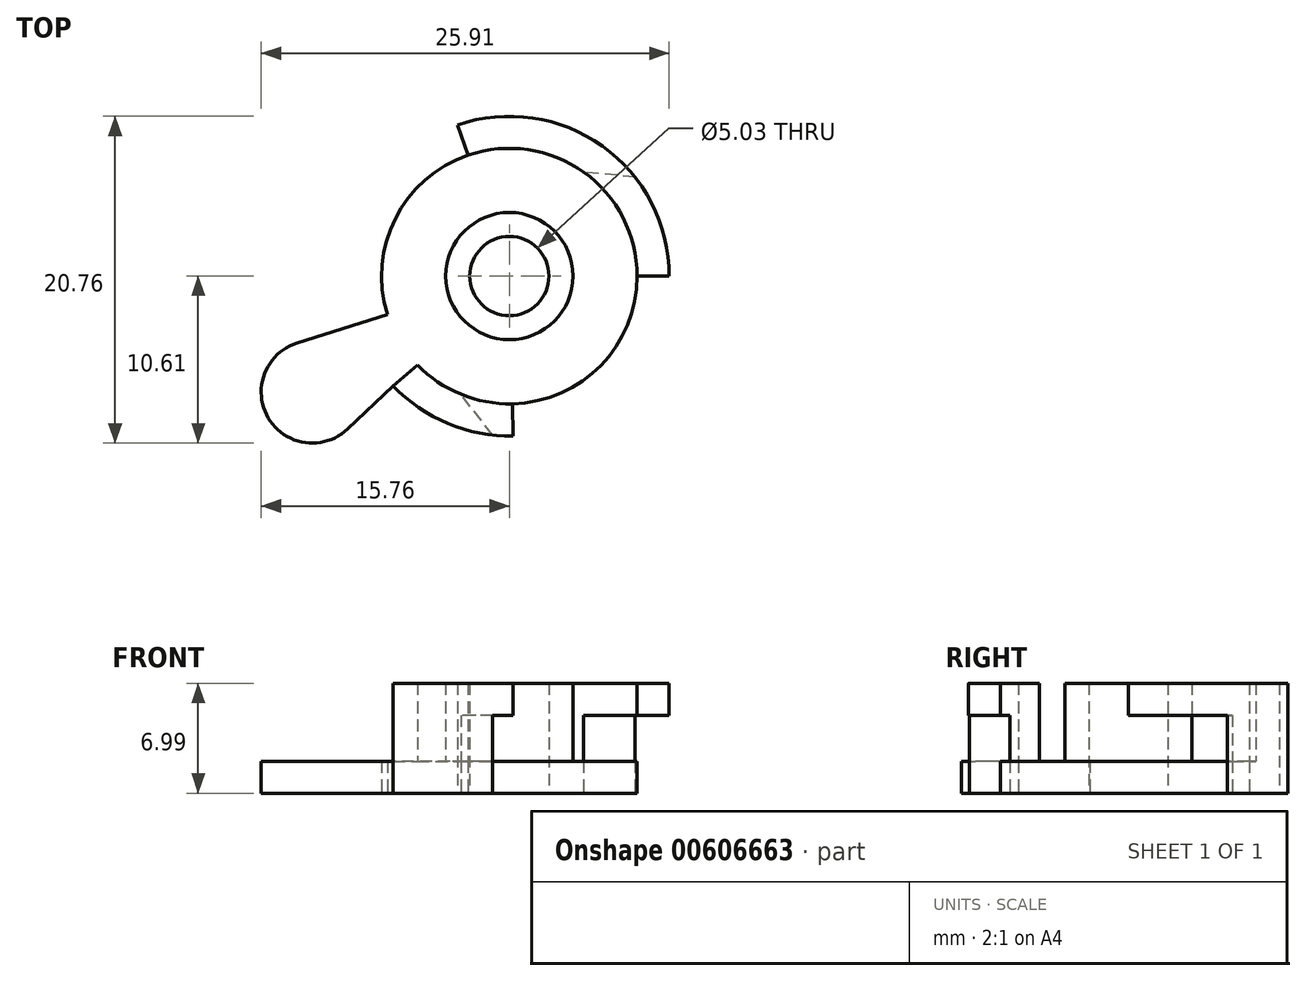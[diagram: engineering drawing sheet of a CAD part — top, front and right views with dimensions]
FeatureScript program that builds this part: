
annotation { "Feature Type Name" : "Feature", "Feature Type Description" : "" }
export const myFeature = defineFeature(function(context is Context, id is Id, definition is map)
    precondition{}
    {
        {
            var Q0;
            Q0=qCreatedBy(makeId("Top.planeOp"),FACE);
            var sketch = newSketch(context, id + "F0", { "sketchPlane" : qUnion([Q0])});
            skCircle(sketch, "E0", {"center": v(0, 0) * mm, "radius": 8.12 * mm});
            skCircle(sketch, "E1", {"center": v(0, 0) * mm, "radius": 2.51 * mm});
            skArc(sketch, "E2", {"start": v(10.15, 0) * mm, "mid": v(5.9, 8.26) * mm, "end": v(-3.28, 9.6) * mm});
            skLineSegment(sketch, "E3", {"start": v(-3.28, 9.6) * mm, "end": v(-2.63, 7.68) * mm});
            skLineSegment(sketch, "E4", {"start": v(10.15, 0) * mm, "end": v(8.12, 0) * mm});
            skArc(sketch, "E5", {"start": v(-9.68, -3.05) * mm, "mid": v(-5.9, -8.26) * mm, "end": v(0.24, -10.14) * mm});
            skLineSegment(sketch, "E6", {"start": v(-9.68, -3.05) * mm, "end": v(-7.74, -2.44) * mm});
            skLineSegment(sketch, "E7", {"start": v(-7.37, -6.97) * mm, "end": v(-10.28, -9.72) * mm});
            skLineSegment(sketch, "E8", {"start": v(-9.68, -3.05) * mm, "end": v(-13.5, -4.26) * mm});
            skLineSegment(sketch, "E9", {"start": v(0.24, -10.14) * mm, "end": v(0.2, -8.11) * mm});
            skLineSegment(sketch, "E10", {"start": v(-5.9, -8.26) * mm, "end": v(0, 0) * mm, "construction": true});
            skPoint(sketch, "E10.startSnap0", {"position": v(-5.9, -8.26) * mm});
            skLineSegment(sketch, "E11", {"start": v(5.9, 8.26) * mm, "end": v(0, 0) * mm, "construction": true});
            skLineSegment(sketch, "E12", {"start": v(-5.9, -8.26) * mm, "end": v(4.72, 6.6) * mm, "construction": true});
            skLineSegment(sketch, "E13", {"start": v(-8.75, -5.14) * mm, "end": v(-15.31, -9) * mm, "construction": true});
            skArc(sketch, "E14", {"start": v(-13.5, -4.26) * mm, "mid": v(-15.31, -9) * mm, "end": v(-10.28, -9.72) * mm});
            skSolve(sketch);
        }
        {
            var Q0;
            Q0=makeQuery(id+"F0.imprint","IMPRINT",FACE,{"disambiguationData":[TD([[makeQuery(id+"F0.imprint","IMPRINT",EDGE,{"derivedFrom":sQuery(id+"F0.wireOp",EDGE,"E1")}),-1.0]])]});
            var Q1;
            Q1=makeQuery(id+"F0.imprint","IMPRINT",FACE,{"disambiguationData":[TD([[makeQuery(id+"F0.imprint","IMPRINT",EDGE,{"derivedFrom":sQuery(id+"F0.wireOp",EDGE,"E2")}),1.0]])]});
            var Q2;
            {var subQ0=sQuery(id+"F0.wireOp",EDGE,"E6");Q2=makeQuery(id+"F0.imprint","IMPRINT",FACE,{"disambiguationData":[TD([[makeQuery(id+"F0.imprint","IMPRINT",EDGE,{"derivedFrom":subQ0}),-1.0]])]});}
            var Q3;
            {var subQ2=sQuery(id+"F0.wireOp",EDGE,"E7");Q3=makeQuery(id+"F0.imprint","IMPRINT",FACE,{"disambiguationData":[TD([[makeQuery(id+"F0.imprint","IMPRINT",EDGE,{"derivedFrom":subQ2}),-1.0]])]});}
            extrude(context, id + "F1", {"entities" : qUnion([Q0, Q1, Q2, Q3]), "depth" : 2.03 * mm, "offsetDistance" : 25.4 * mm});
        }
        {
            var Q0;
            Q0=makeQuery(id+"F1.opExtrude","CAP_FACE",FACE,{"disambiguationData":[OSD([sQuery(id+"F0.wireOp",EDGE,"E0"),sQuery(id+"F0.wireOp",EDGE,"E1"),sQuery(id+"F0.wireOp",EDGE,"E2"),sQuery(id+"F0.wireOp",EDGE,"E3"),sQuery(id+"F0.wireOp",EDGE,"E4"),sQuery(id+"F0.wireOp",EDGE,"E5"),sQuery(id+"F0.wireOp",EDGE,"E6"),sQuery(id+"F0.wireOp",EDGE,"E7"),sQuery(id+"F0.wireOp",EDGE,"E8"),sQuery(id+"F0.wireOp",EDGE,"E9"),sQuery(id+"F0.wireOp",EDGE,"E14")])],"isStart":false});
            var sketch = newSketch(context, id + "F2", { "sketchPlane" : qUnion([Q0])});
            skCircle(sketch, "E15", {"center": v(0, 0) * mm, "radius": 4.04 * mm});
            skCircle(sketch, "E16", {"center": v(0, 0) * mm, "radius": 2.51 * mm});
            skArc(sketch, "E17", {"start": v(-7.37, -6.97) * mm, "mid": v(-3.9, -9.37) * mm, "end": v(0.24, -10.14) * mm});
            skArc(sketch, "E18", {"start": v(10.15, 0) * mm, "mid": v(5.9, 8.26) * mm, "end": v(-3.28, 9.6) * mm});
            skCircle(sketch, "E19", {"center": v(0, 0) * mm, "radius": 8.12 * mm});
            skLineSegment(sketch, "E20", {"start": v(0.24, -10.14) * mm, "end": v(0.2, -8.11) * mm});
            skLineSegment(sketch, "E21", {"start": v(-7.37, -6.97) * mm, "end": v(-5.84, -5.63) * mm});
            skLineSegment(sketch, "E22", {"start": v(-3.28, 9.6) * mm, "end": v(-2.63, 7.68) * mm});
            skLineSegment(sketch, "E23", {"start": v(10.15, 0) * mm, "end": v(8.12, 0) * mm});
            skSolve(sketch);
        }
        {
            var Q0;
            Q0=makeQuery(id+"F2.imprint","IMPRINT",FACE,{"disambiguationData":[TD([[makeQuery(id+"F2.imprint","IMPRINT",EDGE,{"derivedFrom":sQuery(id+"F2.wireOp",EDGE,"E17")}),1.0]])]});
            var Q1;
            Q1=makeQuery(id+"F2.imprint","IMPRINT",FACE,{"disambiguationData":[TD([[makeQuery(id+"F2.imprint","IMPRINT",EDGE,{"derivedFrom":sQuery(id+"F2.wireOp",EDGE,"E15")}),1.0]])]});
            var Q2;
            Q2=makeQuery(id+"F2.imprint","IMPRINT",FACE,{"disambiguationData":[TD([[makeQuery(id+"F2.imprint","IMPRINT",EDGE,{"derivedFrom":sQuery(id+"F2.wireOp",EDGE,"E18")}),1.0]])]});
            extrude(context, id + "F3", {"entities" : qUnion([Q0, Q1, Q2]), "operationType" : NewBodyOperationType.ADD, "depth" : 4.95 * mm, "offsetDistance" : 25.4 * mm});
        }
        {
            var Q0;
            Q0=makeQuery(id+"F1.opExtrude","CAP_FACE",FACE,{"disambiguationData":[OSD([sQuery(id+"F0.wireOp",EDGE,"E0"),sQuery(id+"F0.wireOp",EDGE,"E1"),sQuery(id+"F0.wireOp",EDGE,"E2"),sQuery(id+"F0.wireOp",EDGE,"E3"),sQuery(id+"F0.wireOp",EDGE,"E4"),sQuery(id+"F0.wireOp",EDGE,"E5"),sQuery(id+"F0.wireOp",EDGE,"E6"),sQuery(id+"F0.wireOp",EDGE,"E7"),sQuery(id+"F0.wireOp",EDGE,"E8"),sQuery(id+"F0.wireOp",EDGE,"E9"),sQuery(id+"F0.wireOp",EDGE,"E14")])],"isStart":true});
            var sketch = newSketch(context, id + "F4", { "sketchPlane" : qUnion([Q0])});
            skLineSegment(sketch, "E24", {"start": v(10.15, 0) * mm, "end": v(8.12, 0) * mm});
            skArc(sketch, "E25", {"start": v(7.97, -6.29) * mm, "mid": v(9.59, -3.33) * mm, "end": v(10.15, 0) * mm});
            skCircle(sketch, "E26", {"center": v(0, 0) * mm, "radius": 8.12 * mm});
            skLineSegment(sketch, "E27", {"start": v(0.24, 10.14) * mm, "end": v(0.2, 8.11) * mm});
            skArc(sketch, "E28", {"start": v(0.24, 10.14) * mm, "mid": v(-0.42, 10.14) * mm, "end": v(-1.08, 10.09) * mm});
            skLineSegment(sketch, "E29", {"start": v(-1.08, 10.09) * mm, "end": v(-3.08, 7.51) * mm});
            skLineSegment(sketch, "E30", {"start": v(-3.08, 7.51) * mm, "end": v(-9.84, 4.74) * mm, "construction": true});
            skLineSegment(sketch, "E31", {"start": v(7.97, -6.29) * mm, "end": v(4.72, -6.6) * mm});
            skLineSegment(sketch, "E32", {"start": v(4.72, -6.6) * mm, "end": v(-3.74, -12.65) * mm, "construction": true});
            skSolve(sketch);
        }
        {
            var Q0;
            {var subQ0=sQuery(id+"F4.wireOp",EDGE,"E27");Q0=makeQuery(id+"F4.imprint","IMPRINT",FACE,{"disambiguationData":[TD([[makeQuery(id+"F4.imprint","IMPRINT",EDGE,{"derivedFrom":subQ0}),-1.0]])]});}
            var Q1;
            {var subQ0=sQuery(id+"F4.wireOp",EDGE,"E24");Q1=makeQuery(id+"F4.imprint","IMPRINT",FACE,{"disambiguationData":[TD([[makeQuery(id+"F4.imprint","IMPRINT",EDGE,{"derivedFrom":subQ0}),1.0]])]});}
            extrude(context, id + "F5", {"entities" : qUnion([Q0, Q1]), "operationType" : NewBodyOperationType.REMOVE, "oppositeDirection" : true, "depth" : 4.95 * mm, "offsetDistance" : 25.4 * mm});
        }
    });
